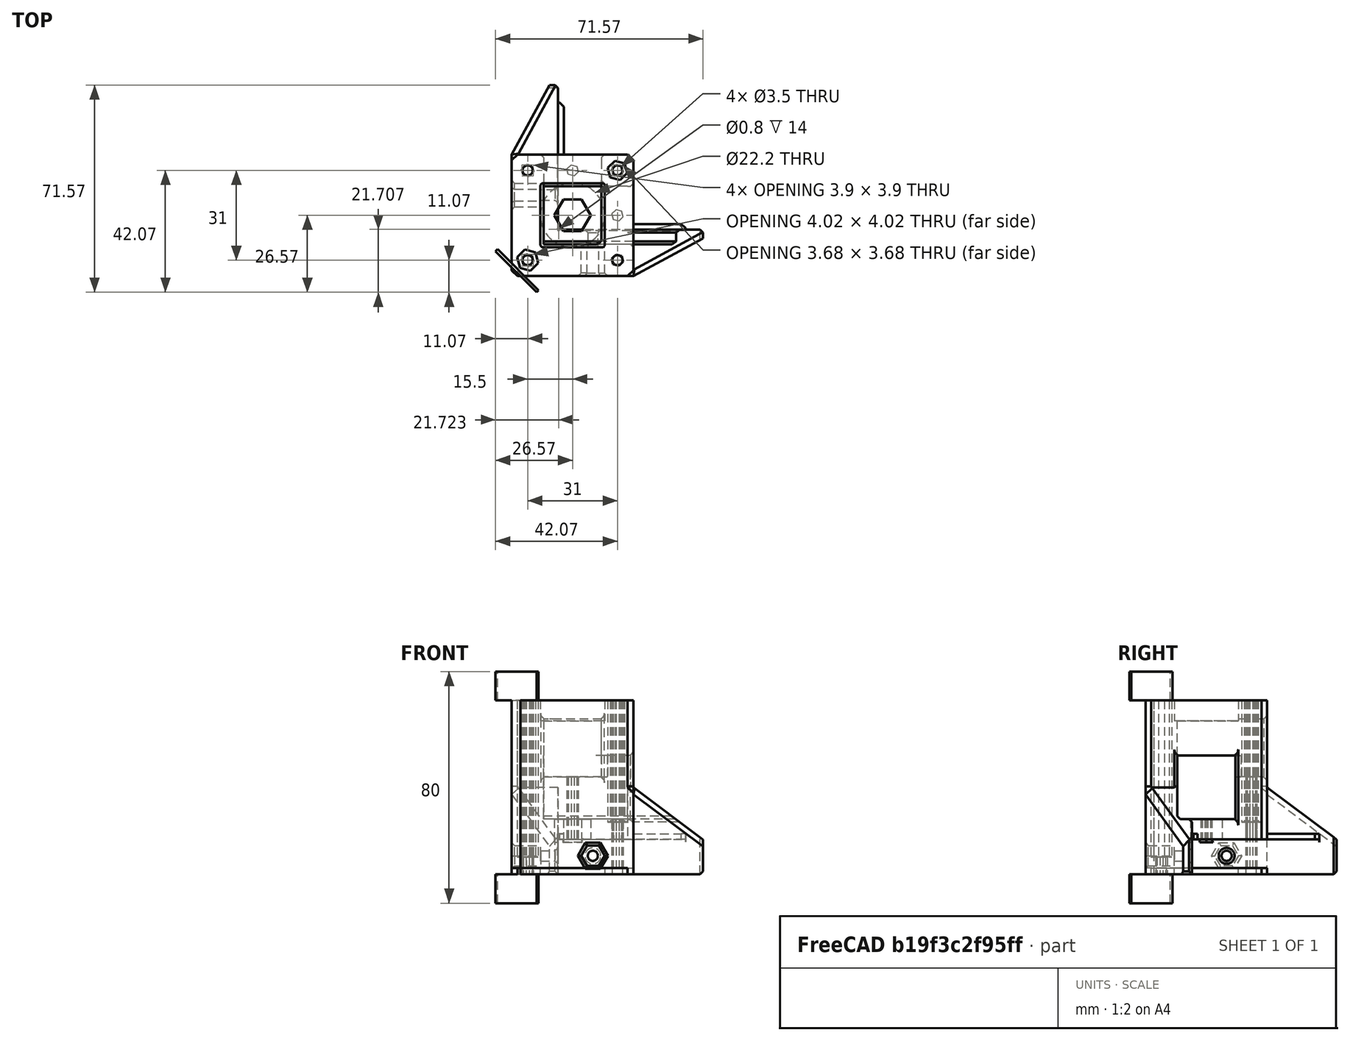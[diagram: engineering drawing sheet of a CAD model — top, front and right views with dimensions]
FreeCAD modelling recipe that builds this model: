
FCSTD DOCUMENT  (FreeCAD 0.19R)
Label: StepperTower_structural
License: All rights reserved
LicenseURL: http://en.wikipedia.org/wiki/All_rights_reserved
objects: Sketcher::SketchObject×27, PartDesign::Pocket×20, PartDesign::Chamfer×18, PartDesign::Fillet×7, PartDesign::Pad×6, PartDesign::Body×2, Mesh::Feature×1
note: 131 computed .brp shape members not serialized (recipe doc carries the construction recipe); baked Part::Feature solids carry a one-line shape summary decoded from their .brp

FEATURE [Sketcher::SketchObject] Sketch  label="wings"
  FullyConstrained = false
  MapMode = 5
  Support = -> [XY_Plane]
  sketch-geometry (21):
    g0: Circle CenterX=5 CenterY=5 CenterZ=0 NormalX=0 NormalY=0 NormalZ=1 AngleXU=0 Radius=2.00199
    g1: LineSegment StartX=-16 StartY=26 StartZ=0 EndX=26 EndY=26 EndZ=0
    g2: LineSegment StartX=26 StartY=26 StartZ=0 EndX=26 EndY=-16 EndZ=0
    g3: LineSegment StartX=26 StartY=-16 StartZ=0 EndX=-16 EndY=-16 EndZ=0
    g4: LineSegment StartX=-16 StartY=-16 StartZ=0 EndX=-16 EndY=26 EndZ=0
    g5: Circle CenterX=20.5 CenterY=20.5 CenterZ=0 NormalX=0 NormalY=0 NormalZ=1 AngleXU=0 Radius=1.5
    g6: Circle CenterX=-10.5 CenterY=20.5 CenterZ=0 NormalX=0 NormalY=0 NormalZ=1 AngleXU=0 Radius=1.5
    g7: Circle CenterX=-10.5 CenterY=-10.5 CenterZ=0 NormalX=0 NormalY=0 NormalZ=1 AngleXU=0 Radius=1.5
    g8: Circle CenterX=20.5 CenterY=-10.5 CenterZ=0 NormalX=0 NormalY=0 NormalZ=1 AngleXU=0 Radius=1.5
    g9: LineSegment StartX=-10.5 StartY=20.5 StartZ=0 EndX=20.5 EndY=20.5 EndZ=0
    g10: LineSegment StartX=20.5 StartY=20.5 StartZ=0 EndX=20.5 EndY=-10.5 EndZ=0
    g11: LineSegment StartX=20.5 StartY=-10.5 StartZ=0 EndX=-10.5 EndY=-10.5 EndZ=0
    g12: LineSegment StartX=-10.5 StartY=-10.5 StartZ=0 EndX=-10.5 EndY=20.5 EndZ=0
    g13: LineSegment StartX=0 StartY=50 StartZ=0 EndX=-3 EndY=50 EndZ=0
    g14: LineSegment StartX=-16 StartY=26 StartZ=0 EndX=-16 EndY=-16 EndZ=0
    g15: LineSegment StartX=-16 StartY=-16 StartZ=0 EndX=26 EndY=-16 EndZ=0
    g16: LineSegment StartX=50 StartY=-3 StartZ=0 EndX=50 EndY=0 EndZ=0
    g17: LineSegment StartX=50 StartY=0 StartZ=0 EndX=0 EndY=0 EndZ=0
    g18: LineSegment StartX=0 StartY=0 StartZ=0 EndX=0 EndY=50 EndZ=0
    g19: LineSegment StartX=-16 StartY=26 StartZ=0 EndX=-3 EndY=50 EndZ=0
    g20: LineSegment StartX=26 StartY=-16 StartZ=0 EndX=50 EndY=-3 EndZ=0
  constraints (55):
    c: DistanceX(g0) = 5
    c: DistanceY(g0) = 5
    c: Coincident(g1,g2)
    c: Coincident(g2,g3)
    c: Coincident(g3,g4)
    c: Coincident(g4,g1)
    c: Horizontal(g1)
    c: Horizontal(g3)
    c: Vertical(g2)
    c: Vertical(g4)
    c: Distance(g1) = 42
    c: Equal(g2,g1)
    c: Symmetric(g1,g3,g0)
    c: Coincident(g9,g6)
    c: Coincident(g9,g5)
    c: Horizontal(g9)
    c: Coincident(g9,g10)
    c: Coincident(g10,g8)
    c: Coincident(g10,g11)
    c: Coincident(g11,g7)
    c: Coincident(g11,g12)
    c: Coincident(g12,g9)
    c: Vertical(g12)
    c: Diameter(g6) = 3
    c: Equal(g6,g5)
    c: Equal(g6,g8)
    c: Equal(g6,g7)
    c: Distance(g11) = 31
    c: Symmetric(g7,g5,g0)
    c: Equal(g11,g12)
    c: Equal(g10,g11)
    c: Equal(g10,g9)
    c: PointOnObject(g13,g-2)
    c: Horizontal(g13)
    c: Vertical(g14)
    c: Coincident(g14,g15)
    c: Horizontal(g15)
    c: Vertical(g16)
    c: Coincident(g16,g17)
    c: Horizontal(g17)
    c: Coincident(g17,g18)
    c: Coincident(g18,g13)
    c: DistanceY(g13) = 50
    c: DistanceX(g16) = 50
    c: DistanceX(g14) = -16
    c: Distance(g13) = 3
    c: Distance(g16) = 3
    c: Coincident(g17,g-1)
    c: DistanceX(g15) = 26
    c: DistanceY(g14) = -16
    c: DistanceY(g14) = 26
    c: Coincident(g19,g14)
    c: Coincident(g19,g13)
    c: Coincident(g20,g15)
    c: Coincident(g20,g16)
FEATURE [Sketcher::SketchObject] Sketch002  label="body"
  FullyConstrained = false
  MapMode = 5
  Placement = pos=(0,0,60) rot=(0,0,1;0rad)
  sketch-geometry (5):
    g0: LineSegment StartX=-16 StartY=26 StartZ=0 EndX=26 EndY=26 EndZ=0
    g1: LineSegment StartX=26 StartY=26 StartZ=0 EndX=26 EndY=-16 EndZ=0
    g2: LineSegment StartX=26 StartY=-16 StartZ=0 EndX=-16 EndY=-16 EndZ=0
    g3: LineSegment StartX=-16 StartY=-16 StartZ=0 EndX=-16 EndY=26 EndZ=0
    g4: Circle CenterX=5 CenterY=5 CenterZ=0 NormalX=0 NormalY=0 NormalZ=1 AngleXU=0 Radius=0.859105
  constraints (13):
    c: Coincident(g0,g1)
    c: Coincident(g1,g2)
    c: Coincident(g2,g3)
    c: Coincident(g3,g0)
    c: Horizontal(g0)
    c: Horizontal(g2)
    c: Vertical(g1)
    c: Vertical(g3)
    c: Distance(g0) = 42
    c: DistanceX(g4) = 5
    c: DistanceY(g4) = 5
    c: Symmetric(g0,g2,g4)
    c: Distance(g1) = 42
FEATURE [Sketcher::SketchObject] Sketch003  label="y-hole"
  FullyConstrained = false
  MapMode = 5
  Placement = pos=(26,0,0) rot=(0.57735,0.57735,0.57735;2.0944rad)
  sketch-geometry (5):
    g0: LineSegment StartX=-5 StartY=41 StartZ=0 EndX=15 EndY=41 EndZ=0
    g1: LineSegment StartX=15 StartY=41 StartZ=0 EndX=15 EndY=19 EndZ=0
    g2: LineSegment StartX=15 StartY=19 StartZ=0 EndX=-5 EndY=19 EndZ=0
    g3: LineSegment StartX=-5 StartY=19 StartZ=0 EndX=-5 EndY=41 EndZ=0
    g4: Circle CenterX=5 CenterY=19 CenterZ=0 NormalX=0 NormalY=0 NormalZ=1 AngleXU=0 Radius=1.08669
  constraints (13):
    c: Coincident(g0,g1)
    c: Coincident(g1,g2)
    c: Coincident(g2,g3)
    c: Coincident(g3,g0)
    c: Horizontal(g0)
    c: Horizontal(g2)
    c: Vertical(g1)
    c: Vertical(g3)
    c: DistanceX(g4) = 5
    c: Symmetric(g1,g2,g4)
    c: DistanceY(g1) = 19
    c: Distance(g1) = 22
    c: Distance(g0) = 20
FEATURE [Sketcher::SketchObject] Sketch004  label="x-hole"
  FullyConstrained = false
  MapMode = 5
  Placement = pos=(0,26,0) rot=(0,0.707107,0.707107;3.14159rad)
  sketch-geometry (5):
    g0: LineSegment StartX=-15 StartY=53.6 StartZ=0 EndX=5 EndY=53.6 EndZ=0
    g1: LineSegment StartX=5 StartY=53.6 StartZ=0 EndX=5 EndY=33.6 EndZ=0
    g2: LineSegment StartX=5 StartY=33.6 StartZ=0 EndX=-15 EndY=33.6 EndZ=0
    g3: LineSegment StartX=-15 StartY=33.6 StartZ=0 EndX=-15 EndY=53.6 EndZ=0
    g4: Circle CenterX=-5 CenterY=33.6 CenterZ=0 NormalX=0 NormalY=0 NormalZ=1 AngleXU=0 Radius=1.47678
  constraints (13):
    c: Coincident(g0,g1)
    c: Coincident(g1,g2)
    c: Coincident(g2,g3)
    c: Coincident(g3,g0)
    c: Horizontal(g0)
    c: Horizontal(g2)
    c: Vertical(g1)
    c: Vertical(g3)
    c: DistanceX(g4) = -5
    c: Symmetric(g1,g2,g4)
    c: Distance(g2) = 20
    c: DistanceY(g1) = 33.6
    c: Distance(g1) = 20
FEATURE [Sketcher::SketchObject] Sketch005  label="RightLholes"
  FullyConstrained = true
  MapMode = 5
  Placement = pos=(0,0,0) rot=(0.57735,0.57735,0.57735;2.0944rad)
  sketch-geometry (2):
    g0: Circle CenterX=12 CenterY=6.35 CenterZ=0 NormalX=0 NormalY=0 NormalZ=1 AngleXU=0 Radius=1.75
    g1: Circle CenterX=37 CenterY=6.35 CenterZ=0 NormalX=0 NormalY=0 NormalZ=1 AngleXU=0 Radius=1.75
  constraints (6):
    c: DistanceY(g0) = 6.35
    c: DistanceX(g0) = 12
    c: Diameter(g0) = 3.5
    c: Distance(g1,g0) = 25
    c: DistanceY(g1) = 6.35
    c: Diameter(g1) = 3.5
FEATURE [Sketcher::SketchObject] Sketch006  label="leftLHoles"
  FullyConstrained = false
  MapMode = 5
  Placement = pos=(0,0,0) rot=(0,0.707107,0.707107;3.14159rad)
  sketch-geometry (6):
    g0: Circle CenterX=-12 CenterY=6.35 CenterZ=0 NormalX=0 NormalY=0 NormalZ=1 AngleXU=0 Radius=1.75
    g1: LineSegment StartX=-7.5 StartY=14.1629 StartZ=0 EndX=-2.5 EndY=14.1629 EndZ=0
    g2: LineSegment StartX=-2.5 StartY=14.1629 StartZ=0 EndX=-2.5 EndY=11.492 EndZ=0
    g3: LineSegment StartX=-2.5 StartY=11.492 StartZ=0 EndX=-7.5 EndY=11.492 EndZ=0
    g4: LineSegment StartX=-7.5 StartY=11.492 StartZ=0 EndX=-7.5 EndY=14.1629 EndZ=0
    g5: Circle CenterX=-37 CenterY=6.35 CenterZ=0 NormalX=0 NormalY=0 NormalZ=1 AngleXU=0 Radius=1.75
  constraints (16):
    c: DistanceX(g0) = -12
    c: DistanceY(g0) = 6.35
    c: Diameter(g0) = 3.5
    c: Coincident(g1,g2)
    c: Coincident(g2,g3)
    c: Coincident(g3,g4)
    c: Coincident(g4,g1)
    c: Horizontal(g1)
    c: Horizontal(g3)
    c: Vertical(g2)
    c: Vertical(g4)
    c: Distance(g3) = 5
    c: DistanceX(g2) = -2.5
    c: Distance(g5,g0) = 25
    c: DistanceY(g5) = 6.35
    c: Diameter(g5) = 3.5
FEATURE [Sketcher::SketchObject] Sketch011  label="bearingHole"
  FullyConstrained = true
  MapMode = 5
  Placement = pos=(0,0,19) rot=(0,0,1;0rad)
  sketch-geometry (7):
    g0: LineSegment StartX=8.14656 StartY=-0.45 StartZ=0 EndX=11.2931 EndY=5 EndZ=0
    g1: LineSegment StartX=11.2931 StartY=5 StartZ=0 EndX=8.14656 EndY=10.45 EndZ=0
    g2: LineSegment StartX=8.14656 StartY=10.45 StartZ=0 EndX=1.85344 EndY=10.45 EndZ=0
    g3: LineSegment StartX=1.85344 StartY=10.45 StartZ=0 EndX=-1.29312 EndY=5 EndZ=0
    g4: LineSegment StartX=-1.29312 StartY=5 StartZ=0 EndX=1.85344 EndY=-0.45 EndZ=0
    g5: LineSegment StartX=1.85344 StartY=-0.45 StartZ=0 EndX=8.14656 EndY=-0.45 EndZ=0
    g6: Circle CenterX=5 CenterY=5 CenterZ=0 NormalX=0 NormalY=0 NormalZ=1 AngleXU=0 Radius=6.29312
  constraints (17):
    c: Coincident(g0,g1)
    c: Coincident(g1,g2)
    c: Coincident(g2,g3)
    c: Coincident(g3,g4)
    c: Coincident(g4,g5)
    c: Coincident(g5,g0)
    c: Equal(g0, g1-g5) x5
    c: PointOnObject(g0,g6)
    c: PointOnObject(g1,g6)
    c: PointOnObject(g2,g6)
    c: PointOnObject(g3,g6)
    c: PointOnObject(g4,g6)
    c: PointOnObject(g5,g6)
    c: Distance(g0,g3) = 10.9
    c: Horizontal(g5)
    c: DistanceX(g6) = 5
    c: DistanceY(g6) = 5
FEATURE [Sketcher::SketchObject] Sketch018  label="FrontStepperBoltClear"
  FullyConstrained = false
  MapMode = 5
  Placement = pos=(0,0,59.7) rot=(0,0,1;0rad)
  sketch-geometry (11):
    g0: Circle CenterX=-10.5 CenterY=20.5 CenterZ=0 NormalX=0 NormalY=0 NormalZ=1 AngleXU=0 Radius=1.4
    g1: Circle CenterX=20.5 CenterY=-10.5 CenterZ=0 NormalX=0 NormalY=0 NormalZ=1 AngleXU=0 Radius=1.4
    g2: Circle CenterX=5 CenterY=5 CenterZ=0 NormalX=0 NormalY=0 NormalZ=1 AngleXU=0 Radius=0.593527
    g3: Circle CenterX=-10.5 CenterY=-10.5 CenterZ=0 NormalX=0 NormalY=0 NormalZ=1 AngleXU=0 Radius=1.75
    g4: LineSegment StartX=20.9931 StartY=18.6597 StartZ=0 EndX=22.3403 EndY=20.0069 EndZ=0
    g5: LineSegment StartX=22.3403 StartY=20.0069 StartZ=0 EndX=21.8472 EndY=21.8472 EndZ=0
    g6: LineSegment StartX=21.8472 StartY=21.8472 StartZ=0 EndX=20.0069 EndY=22.3403 EndZ=0
    g7: LineSegment StartX=20.0069 StartY=22.3403 StartZ=0 EndX=18.6597 EndY=20.9931 EndZ=0
    g8: LineSegment StartX=18.6597 StartY=20.9931 StartZ=0 EndX=19.1528 EndY=19.1528 EndZ=0
    g9: LineSegment StartX=19.1528 StartY=19.1528 StartZ=0 EndX=20.9931 EndY=18.6597 EndZ=0
    g10: Circle CenterX=20.5 CenterY=20.5 CenterZ=0 NormalX=0 NormalY=0 NormalZ=1 AngleXU=0 Radius=1.90526
  constraints (27):
    c: Diameter(g0) = 2.8
    c: Diameter(g1) = 2.8
    c: DistanceX(g2) = 5
    c: DistanceY(g2) = 5
    c: Symmetric(g1,g0,g2)
    c: DistanceY(g0) = 20.5
    c: DistanceX(g0) = -10.5
    c: DistanceX(g3) = -10.5
    c: DistanceY(g3) = -10.5
    c: Diameter(g3) = 3.5
    c: Coincident(g4,g5)
    c: Coincident(g5,g6)
    c: Coincident(g6,g7)
    c: Coincident(g7,g8)
    c: Coincident(g8,g9)
    c: Coincident(g9,g4)
    c: Equal(g4, g5-g9) x5
    c: PointOnObject(g4,g10)
    c: PointOnObject(g5,g10)
    c: PointOnObject(g6,g10)
    c: PointOnObject(g7,g10)
    c: PointOnObject(g8,g10)
    c: PointOnObject(g9,g10)
    c: Distance(g8,g4) = 3.3
    c: Angle(g4) = 0.785398
    c: DistanceX(g10) = 20.5
    c: DistanceY(g10) = 20.5
FEATURE [Sketcher::SketchObject] Sketch019  label="countersink2"
  FullyConstrained = true
  MapMode = 5
  Placement = pos=(0,-16,0) rot=(1,0,0;1.5708rad)
  sketch-geometry (14):
    g0: LineSegment StartX=39.0207 StartY=2.85 StartZ=0 EndX=41.0415 EndY=6.35 EndZ=0
    g1: LineSegment StartX=41.0415 StartY=6.35 StartZ=0 EndX=39.0207 EndY=9.85 EndZ=0
    g2: LineSegment StartX=39.0207 StartY=9.85 StartZ=0 EndX=34.9793 EndY=9.85 EndZ=0
    g3: LineSegment StartX=34.9793 StartY=9.85 StartZ=0 EndX=32.9585 EndY=6.35 EndZ=0
    g4: LineSegment StartX=32.9585 StartY=6.35 StartZ=0 EndX=34.9793 EndY=2.85 EndZ=0
    g5: LineSegment StartX=34.9793 StartY=2.85 StartZ=0 EndX=39.0207 EndY=2.85 EndZ=0
    g6: Circle CenterX=37 CenterY=6.35 CenterZ=0 NormalX=0 NormalY=0 NormalZ=1 AngleXU=0 Radius=4.04145
    g7: LineSegment StartX=14.0207 StartY=2.85 StartZ=0 EndX=16.0415 EndY=6.35 EndZ=0
    g8: LineSegment StartX=16.0415 StartY=6.35 StartZ=0 EndX=14.0207 EndY=9.85 EndZ=0
    g9: LineSegment StartX=14.0207 StartY=9.85 StartZ=0 EndX=9.97927 EndY=9.85 EndZ=0
    g10: LineSegment StartX=9.97927 StartY=9.85 StartZ=0 EndX=7.95855 EndY=6.35 EndZ=0
    g11: LineSegment StartX=7.95855 StartY=6.35 StartZ=0 EndX=9.97927 EndY=2.85 EndZ=0
    g12: LineSegment StartX=9.97927 StartY=2.85 StartZ=0 EndX=14.0207 EndY=2.85 EndZ=0
    g13: Circle CenterX=12 CenterY=6.35 CenterZ=0 NormalX=0 NormalY=0 NormalZ=1 AngleXU=0 Radius=4.04145
  constraints (34):
    c: Coincident(g0,g1)
    c: Coincident(g1,g2)
    c: Coincident(g2,g3)
    c: Coincident(g3,g4)
    c: Coincident(g4,g5)
    c: Coincident(g5,g0)
    c: Equal(g0, g1-g5) x5
    c: PointOnObject(g0,g6)
    c: PointOnObject(g1,g6)
    c: PointOnObject(g2,g6)
    c: PointOnObject(g3,g6)
    c: PointOnObject(g4,g6)
    c: PointOnObject(g5,g6)
    c: Horizontal(g5)
    c: DistanceY(g6) = 6.35
    c: DistanceX(g6) = 37
    c: Distance(g0,g4) = 7
    c: Coincident(g7,g8)
    c: Coincident(g8,g9)
    c: Coincident(g9,g10)
    c: Coincident(g10,g11)
    c: Coincident(g11,g12)
    c: Coincident(g12,g7)
    c: Equal(g7, g8-g12) x5
    c: PointOnObject(g7,g13)
    c: PointOnObject(g8,g13)
    c: PointOnObject(g9,g13)
    c: PointOnObject(g10,g13)
    c: PointOnObject(g11,g13)
    c: PointOnObject(g12,g13)
    c: Horizontal(g12)
    c: Distance(g7,g11) = 7
    c: DistanceX(g13) = 12
    c: DistanceY(g13) = 6.35
FEATURE [Sketcher::SketchObject] Sketch020  label="countersink1"
  FullyConstrained = true
  MapMode = 5
  Placement = pos=(-16,0,0) rot=(0.57735,-0.57735,-0.57735;2.0944rad)
  sketch-geometry (14):
    g0: LineSegment StartX=-34.9793 StartY=2.85 StartZ=0 EndX=-32.9585 EndY=6.35 EndZ=0
    g1: LineSegment StartX=-32.9585 StartY=6.35 StartZ=0 EndX=-34.9793 EndY=9.85 EndZ=0
    g2: LineSegment StartX=-34.9793 StartY=9.85 StartZ=0 EndX=-39.0207 EndY=9.85 EndZ=0
    g3: LineSegment StartX=-39.0207 StartY=9.85 StartZ=0 EndX=-41.0415 EndY=6.35 EndZ=0
    g4: LineSegment StartX=-41.0415 StartY=6.35 StartZ=0 EndX=-39.0207 EndY=2.85 EndZ=0
    g5: LineSegment StartX=-39.0207 StartY=2.85 StartZ=0 EndX=-34.9793 EndY=2.85 EndZ=0
    g6: Circle CenterX=-37 CenterY=6.35 CenterZ=0 NormalX=0 NormalY=0 NormalZ=1 AngleXU=0 Radius=4.04145
    g7: LineSegment StartX=-9.97927 StartY=2.85 StartZ=0 EndX=-7.95855 EndY=6.35 EndZ=0
    g8: LineSegment StartX=-7.95855 StartY=6.35 StartZ=0 EndX=-9.97927 EndY=9.85 EndZ=0
    g9: LineSegment StartX=-9.97927 StartY=9.85 StartZ=0 EndX=-14.0207 EndY=9.85 EndZ=0
    g10: LineSegment StartX=-14.0207 StartY=9.85 StartZ=0 EndX=-16.0415 EndY=6.35 EndZ=0
    g11: LineSegment StartX=-16.0415 StartY=6.35 StartZ=0 EndX=-14.0207 EndY=2.85 EndZ=0
    g12: LineSegment StartX=-14.0207 StartY=2.85 StartZ=0 EndX=-9.97927 EndY=2.85 EndZ=0
    g13: Circle CenterX=-12 CenterY=6.35 CenterZ=0 NormalX=0 NormalY=0 NormalZ=1 AngleXU=0 Radius=4.04145
  constraints (34):
    c: Coincident(g0,g1)
    c: Coincident(g1,g2)
    c: Coincident(g2,g3)
    c: Coincident(g3,g4)
    c: Coincident(g4,g5)
    c: Coincident(g5,g0)
    c: Equal(g0, g1-g5) x5
    c: PointOnObject(g0,g6)
    c: PointOnObject(g1,g6)
    c: PointOnObject(g2,g6)
    c: PointOnObject(g3,g6)
    c: PointOnObject(g4,g6)
    c: PointOnObject(g5,g6)
    c: Horizontal(g5)
    c: Distance(g0,g3) = 7
    c: DistanceX(g6) = -37
    c: DistanceY(g6) = 6.35
    c: Coincident(g7,g8)
    c: Coincident(g8,g9)
    c: Coincident(g9,g10)
    c: Coincident(g10,g11)
    c: Coincident(g11,g12)
    c: Coincident(g12,g7)
    c: Equal(g7, g8-g12) x5
    c: PointOnObject(g7,g13)
    c: PointOnObject(g8,g13)
    c: PointOnObject(g9,g13)
    c: PointOnObject(g10,g13)
    c: PointOnObject(g11,g13)
    c: PointOnObject(g12,g13)
    c: Horizontal(g12)
    c: Distance(g7,g10) = 7
    c: DistanceX(g13) = -12
    c: DistanceY(g13) = 6.35
FEATURE [Sketcher::SketchObject] Sketch024
  FullyConstrained = false
  MapMode = 5
  Support = -> [XY_Plane001]
  sketch-geometry (5):
    g0: LineSegment StartX=-16 StartY=26 StartZ=0 EndX=26 EndY=26 EndZ=0
    g1: LineSegment StartX=26 StartY=26 StartZ=0 EndX=26 EndY=-16 EndZ=0
    g2: LineSegment StartX=26 StartY=-16 StartZ=0 EndX=-16 EndY=-16 EndZ=0
    g3: LineSegment StartX=-16 StartY=-16 StartZ=0 EndX=-16 EndY=26 EndZ=0
    g4: Circle CenterX=5 CenterY=5 CenterZ=0 NormalX=0 NormalY=0 NormalZ=1 AngleXU=0 Radius=1.67343
  constraints (13):
    c: Coincident(g0,g1)
    c: Coincident(g1,g2)
    c: Coincident(g2,g3)
    c: Coincident(g3,g0)
    c: Horizontal(g0)
    c: Horizontal(g2)
    c: Vertical(g1)
    c: Vertical(g3)
    c: Equal(g0,g1)
    c: Distance(g1) = 42
    c: DistanceX(g4) = 5
    c: DistanceY(g4) = 5
    c: Symmetric(g2,g0,g4)
FEATURE [PartDesign::Pad] Pad002
  Direction = (1,1,1)
  Length = 2.2
  Length2 = 100
  Profile = -> Sketch024
  Type = 0
FEATURE [Sketcher::SketchObject] Sketch025
  FullyConstrained = true
  MapMode = 5
  Placement = pos=(0,0,2.2) rot=(0,0,1;0rad)
  Support = -> [Pad002]
  sketch-geometry (1):
    g0: Circle CenterX=5 CenterY=5 CenterZ=0 NormalX=0 NormalY=0 NormalZ=1 AngleXU=0 Radius=11.1
  constraints (3):
    c: DistanceX(g0) = 5
    c: DistanceY(g0) = 5
    c: Diameter(g0) = 22.2
FEATURE [PartDesign::Pocket] Pocket012
  BaseFeature = -> Pad002
  Length = 5
  Length2 = 100
  Profile = -> Sketch025
  Type = 0
FEATURE [PartDesign::Chamfer] Chamfer
  Angle = 45
  Base = -> Pocket012 [Edge2,Edge8,Edge5,Edge1]
  BaseFeature = -> Pocket012
  ChamferType = 0
  FlipDirection = false
  Size = 2
  Size2 = 1
  SupportTransform = false
FEATURE [Sketcher::SketchObject] Sketch026
  FullyConstrained = false
  MapMode = 5
  Placement = pos=(0,0,2.2) rot=(0,0,1;0rad)
  Support = -> [Chamfer]
  sketch-geometry (9):
    g0: Circle CenterX=-10.5 CenterY=20.5 CenterZ=0 NormalX=0 NormalY=0 NormalZ=1 AngleXU=0 Radius=1.75
    g1: Circle CenterX=20.5 CenterY=20.5 CenterZ=0 NormalX=0 NormalY=0 NormalZ=1 AngleXU=0 Radius=1.75
    g2: Circle CenterX=20.5 CenterY=-10.5 CenterZ=0 NormalX=0 NormalY=0 NormalZ=1 AngleXU=0 Radius=1.75
    g3: Circle CenterX=-10.5 CenterY=-10.5 CenterZ=0 NormalX=0 NormalY=0 NormalZ=1 AngleXU=0 Radius=1.75
    g4: LineSegment StartX=-10.5 StartY=20.5 StartZ=0 EndX=20.5 EndY=20.5 EndZ=0
    g5: LineSegment StartX=20.5 StartY=20.5 StartZ=0 EndX=20.5 EndY=-10.5 EndZ=0
    g6: LineSegment StartX=20.5 StartY=-10.5 StartZ=0 EndX=-10.5 EndY=-10.5 EndZ=0
    g7: LineSegment StartX=-10.5 StartY=-10.5 StartZ=0 EndX=-10.5 EndY=20.5 EndZ=0
    g8: Circle CenterX=5 CenterY=5 CenterZ=0 NormalX=0 NormalY=0 NormalZ=1 AngleXU=0 Radius=0.497796
  constraints (21):
    c: Coincident(g4,g0)
    c: Coincident(g4,g1)
    c: Horizontal(g4)
    c: Coincident(g4,g5)
    c: Coincident(g5,g2)
    c: Coincident(g5,g6)
    c: Horizontal(g6)
    c: Coincident(g6,g7)
    c: Coincident(g7,g4)
    c: Vertical(g7)
    c: Coincident(g3,g6)
    c: Equal(g5,g4)
    c: Distance(g4) = 31
    c: DistanceX(g8) = 5
    c: DistanceY(g8) = 5
    c: Symmetric(g3,g1,g8)
    c: Vertical(g5)
    c: Diameter(g1) = 3.5
    c: Equal(g1,g0)
    c: Equal(g1,g3)
    c: Equal(g1,g2)
FEATURE [PartDesign::Pocket] Pocket013
  BaseFeature = -> Chamfer
  Length = 5
  Length2 = 100
  Profile = -> Sketch026
  Type = 0
FEATURE [PartDesign::Body] Body001  label="Washer"
  Group = -> [Sketch024,Pad002,Sketch025,Pocket012,Chamfer,Sketch026,Pocket013]
  Origin = -> Origin001
  Tip = -> Pocket013
FEATURE [PartDesign::Pad] Pad
  Direction = (1,1,1)
  Length = 60
  Length2 = 100
  Profile = -> Sketch
  Type = 0
FEATURE [PartDesign::Pad] Pad003
  BaseFeature = -> Pad
  Direction = (1,1,1)
  Length = 48
  Length2 = 100
  Profile = -> Sketch002
  Reversed = true
  Type = 0
FEATURE [Sketcher::SketchObject] Sketch032  label="wingcut2"
  FullyConstrained = false
  MapMode = 5
  Placement = pos=(0,0,0) rot=(0.57735,0.57735,0.57735;2.0944rad)
  sketch-geometry (4):
    g0: LineSegment StartX=50 StartY=12 StartZ=0 EndX=26 EndY=30 EndZ=0
    g1: LineSegment StartX=26 StartY=30 StartZ=0 EndX=26 EndY=79.987 EndZ=0
    g2: LineSegment StartX=26 StartY=79.987 StartZ=0 EndX=78.9408 EndY=64.2519 EndZ=0
    g3: LineSegment StartX=78.9408 StartY=64.2519 StartZ=0 EndX=50 EndY=12 EndZ=0
  constraints (9):
    c: Coincident(g0,g1)
    c: Vertical(g1)
    c: Coincident(g1,g2)
    c: Coincident(g2,g3)
    c: Coincident(g3,g0)
    c: DistanceX(g0) = 50
    c: DistanceY(g0) = 12
    c: DistanceX(g0) = 26
    c: DistanceY(g0) = 30
FEATURE [Sketcher::SketchObject] Sketch033  label="WingRidge1"
  FullyConstrained = true
  MapMode = 5
  Placement = pos=(0,26,0) rot=(0,0.707107,0.707107;3.14159rad)
  sketch-geometry (4):
    g0: LineSegment StartX=0 StartY=12 StartZ=0 EndX=-2 EndY=12 EndZ=0
    g1: LineSegment StartX=-2 StartY=12 StartZ=0 EndX=-2 EndY=14 EndZ=0
    g2: LineSegment StartX=-2 StartY=14 StartZ=0 EndX=0 EndY=14 EndZ=0
    g3: LineSegment StartX=0 StartY=14 StartZ=0 EndX=0 EndY=12 EndZ=0
  constraints (12):
    c: PointOnObject(g0,g-2)
    c: Coincident(g0,g1)
    c: Coincident(g1,g2)
    c: PointOnObject(g2,g-2)
    c: Coincident(g2,g3)
    c: Coincident(g3,g0)
    c: Horizontal(g0)
    c: Distance(g0) = 2
    c: Distance(g1) = 2
    c: Vertical(g1)
    c: Distance(g3) = 2
    c: DistanceY(g0) = 12
FEATURE [Sketcher::SketchObject] Sketch034  label="wingridge2"
  FullyConstrained = true
  MapMode = 5
  Placement = pos=(26,0,0) rot=(0.57735,0.57735,0.57735;2.0944rad)
  sketch-geometry (4):
    g0: LineSegment StartX=0 StartY=12 StartZ=0 EndX=2 EndY=12 EndZ=0
    g1: LineSegment StartX=2 StartY=12 StartZ=0 EndX=2 EndY=14 EndZ=0
    g2: LineSegment StartX=2 StartY=14 StartZ=0 EndX=0 EndY=14 EndZ=0
    g3: LineSegment StartX=0 StartY=14 StartZ=0 EndX=0 EndY=12 EndZ=0
  constraints (12):
    c: PointOnObject(g0,g-2)
    c: Coincident(g0,g1)
    c: Coincident(g1,g2)
    c: PointOnObject(g2,g-2)
    c: Coincident(g2,g3)
    c: Coincident(g3,g0)
    c: Horizontal(g0)
    c: Distance(g0) = 2
    c: Distance(g1) = 2
    c: Vertical(g1)
    c: Distance(g3) = 2
    c: DistanceY(g0) = 12
FEATURE [PartDesign::Pad] Pad004
  BaseFeature = -> Pad003
  Direction = (1,1,1)
  Length = 18
  Length2 = 100
  Profile = -> Sketch034
  Type = 0
FEATURE [PartDesign::Pad] Pad005
  BaseFeature = -> Pad004
  Direction = (1,1,1)
  Length = 18
  Length2 = 100
  Profile = -> Sketch033
  Type = 0
FEATURE [PartDesign::Pocket] Pocket
  BaseFeature = -> Pad005
  Length = 23
  Length2 = 100
  Profile = -> Sketch032
  Type = 4
FEATURE [Sketcher::SketchObject] Sketch031  label="WingCut1"
  FullyConstrained = false
  MapMode = 5
  Placement = pos=(0,0,0) rot=(0,0.707107,0.707107;3.14159rad)
  Support = -> [Pocket]
  sketch-geometry (4):
    g0: LineSegment StartX=-50 StartY=12 StartZ=0 EndX=-26 EndY=30 EndZ=0
    g1: LineSegment StartX=-26 StartY=30 StartZ=0 EndX=-26 EndY=75.2135 EndZ=0
    g2: LineSegment StartX=-26 StartY=75.2135 StartZ=0 EndX=-50 EndY=66.3047 EndZ=0
    g3: LineSegment StartX=-50 StartY=66.3047 StartZ=0 EndX=-50 EndY=12 EndZ=0
  constraints (10):
    c: Coincident(g0,g1)
    c: Vertical(g1)
    c: Coincident(g1,g2)
    c: Coincident(g2,g3)
    c: Coincident(g3,g0)
    c: Vertical(g3)
    c: DistanceY(g0) = 12
    c: DistanceX(g0) = -50
    c: DistanceX(g0) = -26
    c: DistanceY(g0) = 30
FEATURE [PartDesign::Pocket] Pocket014
  BaseFeature = -> Pocket
  Length = 5
  Length2 = 100
  Profile = -> Sketch031
  Type = 1
FEATURE [PartDesign::Pocket] Pocket015
  BaseFeature = -> Pocket014
  Length = 31
  Length2 = 100
  Profile = -> Sketch003
  Type = 4
FEATURE [PartDesign::Pocket] Pocket016
  BaseFeature = -> Pocket015
  Length = 31
  Length2 = 100
  Profile = -> Sketch004
  Type = 0
FEATURE [PartDesign::Pocket] Pocket017
  BaseFeature = -> Pocket016
  Length = 5
  Length2 = 100
  Profile = -> Sketch005
  Type = 1
FEATURE [PartDesign::Pocket] Pocket018
  BaseFeature = -> Pocket017
  Length = 5
  Length2 = 100
  Profile = -> Sketch006
  Type = 1
FEATURE [PartDesign::Pocket] Pocket019
  BaseFeature = -> Pocket018
  Length = 10
  Length2 = 100
  Profile = -> Sketch020
  Type = 0
FEATURE [PartDesign::Pocket] Pocket020
  BaseFeature = -> Pocket019
  Length = 10
  Length2 = 100
  Profile = -> Sketch019
  Type = 0
FEATURE [PartDesign::Pocket] Pocket021
  BaseFeature = -> Pocket020
  Length = 8
  Length2 = 100
  Profile = -> Sketch011
  Type = 0
FEATURE [Sketcher::SketchObject] Sketch016  label="stepperboss"
  FullyConstrained = false
  MapMode = 5
  Placement = pos=(0,0,60) rot=(0,0,1;0rad)
  Support = -> [Pocket021]
  sketch-geometry (5):
    g0: LineSegment StartX=-6.1 StartY=16.1 StartZ=0 EndX=16.1 EndY=16.1 EndZ=0
    g1: LineSegment StartX=16.1 StartY=16.1 StartZ=0 EndX=16.1 EndY=-6.1 EndZ=0
    g2: LineSegment StartX=16.1 StartY=-6.1 StartZ=0 EndX=-6.1 EndY=-6.1 EndZ=0
    g3: LineSegment StartX=-6.1 StartY=-6.1 StartZ=0 EndX=-6.1 EndY=16.1 EndZ=0
    g4: Circle CenterX=5 CenterY=5 CenterZ=0 NormalX=0 NormalY=0 NormalZ=1 AngleXU=0 Radius=1.21473
  constraints (13):
    c: Coincident(g0,g1)
    c: Coincident(g1,g2)
    c: Coincident(g2,g3)
    c: Coincident(g3,g0)
    c: Horizontal(g0)
    c: Horizontal(g2)
    c: Vertical(g1)
    c: Vertical(g3)
    c: Distance(g3) = 22.2
    c: Equal(g3,g0)
    c: Symmetric(g0,g2,g4)
    c: DistanceY(g4) = 5
    c: DistanceX(g4) = 5
FEATURE [PartDesign::Pocket] Pocket022
  BaseFeature = -> Pocket021
  Length = 7
  Length2 = 100
  Profile = -> Sketch016
  Type = 0
FEATURE [Sketcher::SketchObject] Sketch035  label="stepperClearanceHoles"
  FullyConstrained = true
  MapMode = 5
  Placement = pos=(0,0,60) rot=(0,0,1;0rad)
  Support = -> [Pocket022]
  sketch-geometry (21):
    g0: LineSegment StartX=-8.54813 StartY=19.977 StartZ=0 EndX=-9.07113 EndY=21.9289 EndZ=0
    g1: LineSegment StartX=-9.07113 StartY=21.9289 StartZ=0 EndX=-11.023 EndY=22.4519 EndZ=0
    g2: LineSegment StartX=-11.023 StartY=22.4519 StartZ=0 EndX=-12.4519 EndY=21.023 EndZ=0
    g3: LineSegment StartX=-12.4519 StartY=21.023 StartZ=0 EndX=-11.9289 EndY=19.0711 EndZ=0
    g4: LineSegment StartX=-11.9289 StartY=19.0711 StartZ=0 EndX=-9.977 EndY=18.5481 EndZ=0
    g5: LineSegment StartX=-9.977 StartY=18.5481 StartZ=0 EndX=-8.54813 EndY=19.977 EndZ=0
    g6: Circle CenterX=-10.5 CenterY=20.5 CenterZ=0 NormalX=0 NormalY=0 NormalZ=1 AngleXU=0 Radius=2.02073
    g7: LineSegment StartX=21.023 StartY=-12.4519 StartZ=0 EndX=22.4519 EndY=-11.023 EndZ=0
    g8: LineSegment StartX=22.4519 StartY=-11.023 StartZ=0 EndX=21.9289 EndY=-9.07113 EndZ=0
    g9: LineSegment StartX=21.9289 StartY=-9.07113 StartZ=0 EndX=19.977 EndY=-8.54813 EndZ=0
    g10: LineSegment StartX=19.977 StartY=-8.54813 StartZ=0 EndX=18.5481 EndY=-9.977 EndZ=0
    g11: LineSegment StartX=18.5481 StartY=-9.977 StartZ=0 EndX=19.0711 EndY=-11.9289 EndZ=0
    g12: LineSegment StartX=19.0711 StartY=-11.9289 StartZ=0 EndX=21.023 EndY=-12.4519 EndZ=0
    g13: Circle CenterX=20.5 CenterY=-10.5 CenterZ=0 NormalX=0 NormalY=0 NormalZ=1 AngleXU=0 Radius=2.02073
    g14: LineSegment StartX=-8.49236 StartY=-11.0379 StartZ=0 EndX=-9.03031 EndY=-9.03031 EndZ=0
    g15: LineSegment StartX=-9.03031 StartY=-9.03031 StartZ=0 EndX=-11.0379 EndY=-8.49236 EndZ=0
    g16: LineSegment StartX=-11.0379 StartY=-8.49236 StartZ=0 EndX=-12.5076 EndY=-9.96205 EndZ=0
    g17: LineSegment StartX=-12.5076 StartY=-9.96205 StartZ=0 EndX=-11.9697 EndY=-11.9697 EndZ=0
    g18: LineSegment StartX=-11.9697 StartY=-11.9697 StartZ=0 EndX=-9.96205 EndY=-12.5076 EndZ=0
    g19: LineSegment StartX=-9.96205 StartY=-12.5076 StartZ=0 EndX=-8.49236 EndY=-11.0379 EndZ=0
    g20: Circle CenterX=-10.5 CenterY=-10.5 CenterZ=0 NormalX=0 NormalY=0 NormalZ=1 AngleXU=0 Radius=2.07846
  constraints (51):
    c: Coincident(g0,g1)
    c: Coincident(g1,g2)
    c: Coincident(g2,g3)
    c: Coincident(g3,g4)
    c: Coincident(g4,g5)
    c: Coincident(g5,g0)
    c: Equal(g0, g1-g5) x5
    c: PointOnObject(g0,g6)
    c: PointOnObject(g1,g6)
    c: PointOnObject(g2,g6)
    c: PointOnObject(g3,g6)
    c: PointOnObject(g4,g6)
    c: PointOnObject(g5,g6)
    c: Coincident(g7,g8)
    c: Coincident(g8,g9)
    c: Coincident(g9,g10)
    c: Coincident(g10,g11)
    c: Coincident(g11,g12)
    c: Coincident(g12,g7)
    c: Equal(g7, g8-g12) x5
    c: PointOnObject(g7,g13)
    c: PointOnObject(g8,g13)
    c: PointOnObject(g9,g13)
    c: PointOnObject(g10,g13)
    c: PointOnObject(g11,g13)
    c: PointOnObject(g12,g13)
    c: Coincident(g14,g15)
    c: Coincident(g15,g16)
    c: Coincident(g16,g17)
    c: Coincident(g17,g18)
    c: Coincident(g18,g19)
    c: Coincident(g19,g14)
    c: Equal(g14, g15-g19) x5
    c: PointOnObject(g14,g20)
    c: PointOnObject(g15,g20)
    c: PointOnObject(g16,g20)
    c: PointOnObject(g17,g20)
    c: PointOnObject(g18,g20)
    c: PointOnObject(g19,g20)
    c: Distance(g0,g3) = 3.5
    c: Distance(g7,g10) = 3.5
    c: Distance(g18,g16) = 3.6
    c: Angle(g19) = 0.785398
    c: Angle(g7) = 0.785398
    c: Angle(g5) = 0.785398
    c: DistanceY(g6) = 20.5
    c: DistanceX(g6) = -10.5
    c: DistanceX(g20) = -10.5
    c: DistanceY(g20) = -10.5
    c: DistanceY(g13) = -10.5
    c: DistanceX(g13) = 20.5
FEATURE [PartDesign::Pocket] Pocket023
  BaseFeature = -> Pocket022
  Length = 5
  Length2 = 100
  Profile = -> Sketch035
  Type = 1
FEATURE [Sketcher::SketchObject] Sketch036  label="cornerStepperBolthead"
  FullyConstrained = true
  MapMode = 5
  Placement = pos=(0,0,60) rot=(0,0,1;0rad)
  Support = -> [Pocket023]
  sketch-geometry (7):
    g0: LineSegment StartX=-6.8751 StartY=-11.4713 StartZ=0 EndX=-7.84639 EndY=-7.84639 EndZ=0
    g1: LineSegment StartX=-7.84639 StartY=-7.84639 StartZ=0 EndX=-11.4713 EndY=-6.8751 EndZ=0
    g2: LineSegment StartX=-11.4713 StartY=-6.8751 StartZ=0 EndX=-14.1249 EndY=-9.52871 EndZ=0
    g3: LineSegment StartX=-14.1249 StartY=-9.52871 StartZ=0 EndX=-13.1536 EndY=-13.1536 EndZ=0
    g4: LineSegment StartX=-13.1536 StartY=-13.1536 StartZ=0 EndX=-9.52871 EndY=-14.1249 EndZ=0
    g5: LineSegment StartX=-9.52871 StartY=-14.1249 StartZ=0 EndX=-6.8751 EndY=-11.4713 EndZ=0
    g6: Circle CenterX=-10.5 CenterY=-10.5 CenterZ=0 NormalX=0 NormalY=0 NormalZ=1 AngleXU=0 Radius=3.75278
  constraints (17):
    c: Coincident(g0,g1)
    c: Coincident(g1,g2)
    c: Coincident(g2,g3)
    c: Coincident(g3,g4)
    c: Coincident(g4,g5)
    c: Coincident(g5,g0)
    c: Equal(g0, g1-g5) x5
    c: PointOnObject(g0,g6)
    c: PointOnObject(g1,g6)
    c: PointOnObject(g2,g6)
    c: PointOnObject(g3,g6)
    c: PointOnObject(g4,g6)
    c: PointOnObject(g5,g6)
    c: Distance(g0,g3) = 6.5
    c: Angle(g5) = 0.785398
    c: DistanceX(g6) = -10.5
    c: DistanceY(g6) = -10.5
FEATURE [PartDesign::Pocket] Pocket024
  BaseFeature = -> Pocket023
  Length = 54
  Length2 = 100
  Profile = -> Sketch036
  Type = 0
FEATURE [Sketcher::SketchObject] Sketch037  label="MountBoltsNew"
  FullyConstrained = true
  MapMode = 5
  Placement = pos=(0,7.5e-15,33.6) rot=(0,0,1;0rad)
  Support = -> [Pocket024]
  sketch-geometry (14):
    g0: LineSegment StartX=5.523 StartY=18.5481 StartZ=0 EndX=6.95187 EndY=19.977 EndZ=0
    g1: LineSegment StartX=6.95187 StartY=19.977 StartZ=0 EndX=6.42887 EndY=21.9289 EndZ=0
    g2: LineSegment StartX=6.42887 StartY=21.9289 StartZ=0 EndX=4.477 EndY=22.4519 EndZ=0
    g3: LineSegment StartX=4.477 StartY=22.4519 StartZ=0 EndX=3.04813 EndY=21.023 EndZ=0
    g4: LineSegment StartX=3.04813 StartY=21.023 StartZ=0 EndX=3.57113 EndY=19.0711 EndZ=0
    g5: LineSegment StartX=3.57113 StartY=19.0711 StartZ=0 EndX=5.523 EndY=18.5481 EndZ=0
    g6: Circle CenterX=5 CenterY=20.5 CenterZ=0 NormalX=0 NormalY=0 NormalZ=1 AngleXU=0 Radius=2.02073
    g7: LineSegment StartX=21.023 StartY=3.04813 StartZ=0 EndX=22.4519 EndY=4.477 EndZ=0
    g8: LineSegment StartX=22.4519 StartY=4.477 StartZ=0 EndX=21.9289 EndY=6.42887 EndZ=0
    g9: LineSegment StartX=21.9289 StartY=6.42887 StartZ=0 EndX=19.977 EndY=6.95187 EndZ=0
    g10: LineSegment StartX=19.977 StartY=6.95187 StartZ=0 EndX=18.5481 EndY=5.523 EndZ=0
    g11: LineSegment StartX=18.5481 StartY=5.523 StartZ=0 EndX=19.0711 EndY=3.57113 EndZ=0
    g12: LineSegment StartX=19.0711 StartY=3.57113 StartZ=0 EndX=21.023 EndY=3.04813 EndZ=0
    g13: Circle CenterX=20.5 CenterY=5 CenterZ=0 NormalX=0 NormalY=0 NormalZ=1 AngleXU=0 Radius=2.02073
  constraints (34):
    c: Coincident(g0,g1)
    c: Coincident(g1,g2)
    c: Coincident(g2,g3)
    c: Coincident(g3,g4)
    c: Coincident(g4,g5)
    c: Coincident(g5,g0)
    c: Equal(g0, g1-g5) x5
    c: PointOnObject(g0,g6)
    c: PointOnObject(g1,g6)
    c: PointOnObject(g2,g6)
    c: PointOnObject(g3,g6)
    c: PointOnObject(g4,g6)
    c: PointOnObject(g5,g6)
    c: Coincident(g7,g8)
    c: Coincident(g8,g9)
    c: Coincident(g9,g10)
    c: Coincident(g10,g11)
    c: Coincident(g11,g12)
    c: Coincident(g12,g7)
    c: Equal(g7, g8-g12) x5
    c: PointOnObject(g7,g13)
    c: PointOnObject(g8,g13)
    c: PointOnObject(g9,g13)
    c: PointOnObject(g10,g13)
    c: PointOnObject(g11,g13)
    c: PointOnObject(g12,g13)
    c: DistanceY(g13) = 5
    c: DistanceX(g6) = 5
    c: Angle(g7) = 0.785398
    c: Angle(g0) = 0.785398
    c: Distance(g0,g4) = 3.5
    c: Distance(g7,g11) = 3.5
    c: DistanceX(g13) = 20.5
    c: DistanceY(g6) = 20.5
FEATURE [PartDesign::Pocket] Pocket025
  BaseFeature = -> Pocket024
  Length = 5
  Length2 = 100
  Profile = -> Sketch037
  Type = 1
FEATURE [Sketcher::SketchObject] Sketch021  label="FrontstepperboltHead"
  FullyConstrained = true
  MapMode = 5
  Placement = pos=(0,0,60) rot=(0,0,1;0rad)
  Support = -> [Pocket025]
  sketch-geometry (8):
    g0: Circle CenterX=-10.5 CenterY=-10.5 CenterZ=0 NormalX=0 NormalY=0 NormalZ=1 AngleXU=0 Radius=3.5
    g1: LineSegment StartX=21.3966 StartY=17.1539 StartZ=0 EndX=23.8461 EndY=19.6034 EndZ=0
    g2: LineSegment StartX=23.8461 StartY=19.6034 StartZ=0 EndX=22.9495 EndY=22.9495 EndZ=0
    g3: LineSegment StartX=22.9495 StartY=22.9495 StartZ=0 EndX=19.6034 EndY=23.8461 EndZ=0
    g4: LineSegment StartX=19.6034 StartY=23.8461 StartZ=0 EndX=17.1539 EndY=21.3966 EndZ=0
    g5: LineSegment StartX=17.1539 StartY=21.3966 StartZ=0 EndX=18.0505 EndY=18.0505 EndZ=0
    g6: LineSegment StartX=18.0505 StartY=18.0505 StartZ=0 EndX=21.3966 EndY=17.1539 EndZ=0
    g7: Circle CenterX=20.5 CenterY=20.5 CenterZ=0 NormalX=0 NormalY=0 NormalZ=1 AngleXU=0 Radius=3.4641
  constraints (20):
    c: DistanceX(g0) = -10.5
    c: DistanceY(g0) = -10.5
    c: Diameter(g0) = 7
    c: Coincident(g1,g2)
    c: Coincident(g2,g3)
    c: Coincident(g3,g4)
    c: Coincident(g4,g5)
    c: Coincident(g5,g6)
    c: Coincident(g6,g1)
    c: Equal(g1, g2-g6) x5
    c: PointOnObject(g1,g7)
    c: PointOnObject(g2,g7)
    c: PointOnObject(g3,g7)
    c: PointOnObject(g4,g7)
    c: PointOnObject(g5,g7)
    c: PointOnObject(g6,g7)
    c: DistanceY(g7) = 20.5
    c: DistanceX(g7) = 20.5
    c: Distance(g5,g1) = 6
    c: Angle(g1) = 0.785398
FEATURE [PartDesign::Pocket] Pocket026
  BaseFeature = -> Pocket025
  Length = 42
  Length2 = 100
  Profile = -> Sketch021
  Type = 0
FEATURE [PartDesign::Pocket] Pocket027
  BaseFeature = -> Pocket026
  Length = 5
  Length2 = 100
  Profile = -> Sketch018
  Type = 1
FEATURE [PartDesign::Chamfer] Chamfer001
  Angle = 45
  Base = -> Pocket027 [Edge329]
  BaseFeature = -> Pocket027
  ChamferType = 0
  FlipDirection = false
  Size = 2
  Size2 = 1
  SupportTransform = false
FEATURE [PartDesign::Chamfer] Chamfer002
  Angle = 45
  Base = -> Chamfer001 [Edge28]
  BaseFeature = -> Chamfer001
  ChamferType = 0
  FlipDirection = false
  Size = 2
  Size2 = 1
  SupportTransform = false
FEATURE [PartDesign::Chamfer] Chamfer003
  Angle = 45
  Base = -> Chamfer002 [Edge113]
  BaseFeature = -> Chamfer002
  ChamferType = 0
  FlipDirection = false
  Size = 3
  Size2 = 1
  SupportTransform = false
FEATURE [PartDesign::Chamfer] Chamfer004
  Angle = 45
  Base = -> Chamfer003 [Edge119,Edge33]
  BaseFeature = -> Chamfer003
  ChamferType = 0
  FlipDirection = false
  Size = 2
  Size2 = 1
  SupportTransform = false
FEATURE [PartDesign::Chamfer] Chamfer005
  Angle = 45
  Base = -> Chamfer004 [Edge164,Edge49]
  BaseFeature = -> Chamfer004
  ChamferType = 0
  FlipDirection = false
  Size = 2
  Size2 = 1
  SupportTransform = false
FEATURE [Sketcher::SketchObject] Sketch038
  FullyConstrained = true
  MapMode = 5
  Placement = pos=(-14.5,-14.5,0) rot=(0.862856,-0.357407,-0.357407;1.71777rad)
  Support = -> [Chamfer005]
  sketch-geometry (8):
    g0: LineSegment StartX=-10 StartY=70 StartZ=0 EndX=10 EndY=70 EndZ=0
    g1: LineSegment StartX=10 StartY=70 StartZ=0 EndX=10 EndY=60 EndZ=0
    g2: LineSegment StartX=10 StartY=60 StartZ=0 EndX=-10 EndY=60 EndZ=0
    g3: LineSegment StartX=-10 StartY=60 StartZ=0 EndX=-10 EndY=70 EndZ=0
    g4: LineSegment StartX=-10 StartY=0 StartZ=0 EndX=10 EndY=0 EndZ=0
    g5: LineSegment StartX=10 StartY=0 StartZ=0 EndX=10 EndY=-10 EndZ=0
    g6: LineSegment StartX=10 StartY=-10 StartZ=0 EndX=-10 EndY=-10 EndZ=0
    g7: LineSegment StartX=-10 StartY=-10 StartZ=0 EndX=-10 EndY=0 EndZ=0
  constraints (22):
    c: Coincident(g0,g1)
    c: Coincident(g1,g2)
    c: Coincident(g2,g3)
    c: Coincident(g3,g0)
    c: Horizontal(g0)
    c: Vertical(g1)
    c: Vertical(g3)
    c: Coincident(g4,g5)
    c: Coincident(g5,g6)
    c: Coincident(g6,g7)
    c: Coincident(g7,g4)
    c: Horizontal(g4)
    c: Vertical(g5)
    c: Vertical(g7)
    c: Distance(g1) = 10
    c: Distance(g5) = 10
    c: Distance(g4) = 20
    c: Distance(g0) = 20
    c: Symmetric(g1,g2,g-2)
    c: Symmetric(g5,g6,g-2)
    c: DistanceY(g1) = 60
    c: DistanceY(g4) = 0
FEATURE [PartDesign::Pad] Pad006
  BaseFeature = -> Chamfer005
  Direction = (1,1,1)
  Length = 1
  Length2 = 100
  Profile = -> Sketch038
  Reversed = true
  Type = 0
FEATURE [Sketcher::SketchObject] Sketch039
  FullyConstrained = false
  MapMode = 5
  Placement = pos=(0,44,0) rot=(0,0.707107,0.707107;3.14159rad)
  Support = -> [Pad006]
  sketch-geometry (1):
    g0: Circle CenterX=-0.151459 CenterY=11.836 CenterZ=0 NormalX=0 NormalY=0 NormalZ=1 AngleXU=0 Radius=0.375
  constraints (1):
    c: Diameter(g0) = 0.75
FEATURE [PartDesign::Pocket] Pocket028
  BaseFeature = -> Pad006
  Length = 38
  Length2 = 100
  Profile = -> Sketch039
  Type = 0
FEATURE [Sketcher::SketchObject] Sketch040
  FullyConstrained = false
  MapMode = 5
  Placement = pos=(44,0,0) rot=(0.57735,0.57735,0.57735;2.0944rad)
  Support = -> [Pocket028]
  sketch-geometry (1):
    g0: Circle CenterX=0.149498 CenterY=11.8569 CenterZ=0 NormalX=0 NormalY=0 NormalZ=1 AngleXU=0 Radius=0.375
  constraints (1):
    c: Diameter(g0) = 0.75
FEATURE [PartDesign::Pocket] Pocket029
  BaseFeature = -> Pocket028
  Length = 39
  Length2 = 100
  Profile = -> Sketch040
  Type = 0
FEATURE [Sketcher::SketchObject] Sketch041
  FullyConstrained = false
  MapMode = 5
  Placement = pos=(0,0,0) rot=(1,0,0;3.14159rad)
  Support = -> [Pocket029]
  sketch-geometry (1):
    g0: Circle CenterX=0.153431 CenterY=-0.13663 CenterZ=0 NormalX=0 NormalY=0 NormalZ=1 AngleXU=0 Radius=0.4
  constraints (1):
    c: Diameter(g0) = 0.8
FEATURE [PartDesign::Pocket] Pocket030
  BaseFeature = -> Pocket029
  Length = 14
  Length2 = 100
  Profile = -> Sketch041
  Type = 0
FEATURE [Sketcher::SketchObject] Sketch042
  FullyConstrained = false
  MapMode = 5
  Placement = pos=(0,0,12) rot=(1,0,0;3.14159rad)
  Support = -> [Pocket030]
  sketch-geometry (1):
    g0: Circle CenterX=1.47746 CenterY=-1.26246 CenterZ=0 NormalX=0 NormalY=0 NormalZ=1 AngleXU=0 Radius=2.19764
FEATURE [PartDesign::Fillet] Fillet
  Base = -> Pocket030 [Edge345,Edge340,Edge280,Edge275]
  BaseFeature = -> Pocket030
  Radius = 1
  SupportTransform = false
FEATURE [PartDesign::Fillet] Fillet001
  Base = -> Fillet [Edge309,Edge306]
  BaseFeature = -> Fillet
  Radius = 1
  SupportTransform = false
FEATURE [PartDesign::Fillet] Fillet002
  Base = -> Fillet001 [Edge101,Edge65]
  BaseFeature = -> Fillet001
  Radius = 2
  SupportTransform = false
FEATURE [PartDesign::Chamfer] Chamfer006
  Angle = 45
  Base = -> Fillet002 [Edge387,Edge132]
  BaseFeature = -> Fillet002
  ChamferType = 0
  FlipDirection = false
  Size = 1.5
  Size2 = 1
  SupportTransform = false
FEATURE [PartDesign::Chamfer] Chamfer007
  Angle = 45
  Base = -> Chamfer006 [Edge135,Edge132]
  BaseFeature = -> Chamfer006
  ChamferType = 0
  FlipDirection = false
  Size = 1
  Size2 = 1
  SupportTransform = false
FEATURE [PartDesign::Chamfer] Chamfer008
  Angle = 45
  Base = -> Chamfer007 [Edge63]
  BaseFeature = -> Chamfer007
  ChamferType = 0
  FlipDirection = false
  Size = 1
  Size2 = 1
  SupportTransform = false
FEATURE [PartDesign::Chamfer] Chamfer009
  Angle = 45
  Base = -> Chamfer008 [Edge27]
  BaseFeature = -> Chamfer008
  ChamferType = 0
  FlipDirection = false
  Size = 1
  Size2 = 1
  SupportTransform = false
FEATURE [PartDesign::Chamfer] Chamfer010
  Angle = 45
  Base = -> Chamfer009 [Edge267,Edge50]
  BaseFeature = -> Chamfer009
  ChamferType = 0
  FlipDirection = false
  Size = 1
  Size2 = 1
  SupportTransform = false
FEATURE [PartDesign::Chamfer] Chamfer011
  Angle = 45
  Base = -> Chamfer010 [Edge186,Edge185,Edge184,Edge183,Edge182,Edge187]
  BaseFeature = -> Chamfer010
  ChamferType = 0
  FlipDirection = false
  Size = 1
  Size2 = 1
  SupportTransform = false
FEATURE [PartDesign::Chamfer] Chamfer012
  Angle = 45
  Base = -> Chamfer011 [Edge133,Edge138,Edge137,Edge136,Edge135,Edge134]
  BaseFeature = -> Chamfer011
  ChamferType = 0
  FlipDirection = false
  Size = 1
  Size2 = 1
  SupportTransform = false
FEATURE [PartDesign::Chamfer] Chamfer013
  Angle = 45
  Base = -> Chamfer012 [Edge92,Edge133]
  BaseFeature = -> Chamfer012
  ChamferType = 0
  FlipDirection = false
  Size = 1
  Size2 = 1
  SupportTransform = false
FEATURE [PartDesign::Fillet] Fillet003
  Base = -> Chamfer013 [Edge111,Edge113]
  BaseFeature = -> Chamfer013
  Radius = 2
  SupportTransform = false
FEATURE [PartDesign::Fillet] Fillet004
  Base = -> Fillet003 [Edge110]
  BaseFeature = -> Fillet003
  Radius = 1
  SupportTransform = false
FEATURE [PartDesign::Fillet] Fillet005
  Base = -> Fillet004 [Edge100]
  BaseFeature = -> Fillet004
  Radius = 2
  SupportTransform = false
FEATURE [PartDesign::Fillet] Fillet006
  Base = -> Fillet005 [Edge47,Edge45,Edge27]
  BaseFeature = -> Fillet005
  Radius = 1
  SupportTransform = false
FEATURE [PartDesign::Chamfer] Chamfer014
  Angle = 45
  Base = -> Fillet006 [Edge53]
  BaseFeature = -> Fillet006
  ChamferType = 0
  FlipDirection = false
  Size = 1
  Size2 = 1
  SupportTransform = false
FEATURE [PartDesign::Chamfer] Chamfer015
  Angle = 45
  Base = -> Chamfer014 [Edge75]
  BaseFeature = -> Chamfer014
  ChamferType = 0
  FlipDirection = false
  Size = 1
  Size2 = 1
  SupportTransform = false
FEATURE [PartDesign::Chamfer] Chamfer016
  Angle = 45
  Base = -> Chamfer015 [Edge82]
  BaseFeature = -> Chamfer015
  ChamferType = 0
  FlipDirection = false
  Size = 1
  Size2 = 1
  SupportTransform = false
FEATURE [PartDesign::Chamfer] Chamfer017
  Angle = 45
  Base = -> Chamfer016 [Edge143]
  BaseFeature = -> Chamfer016
  ChamferType = 0
  FlipDirection = false
  Size = 1
  Size2 = 1
  SupportTransform = false
FEATURE [PartDesign::Body] Body
  Group = -> [Sketch,Sketch002,Sketch003,Sketch004,Sketch005,Sketch006,Sketch011,Sketch016,Sketch018,Sketch019,Sketch020,Sketch021,Pad,Pad003,Sketch031,Sketch032,Sketch033,Sketch034,Pad004,Pad005,Pocket,Sketch035,Sketch036,Sketch037,Pocket014,Pocket015,Pocket016,Pocket017,Pocket018,Pocket019,Pocket020,Pocket021,Pocket022,Pocket023,Pocket024,Pocket025,Pocket026,Pocket027,Chamfer001,Chamfer002,Chamfer003,+30 more]
  Origin = -> Origin
  Tip = -> Chamfer017
FEATURE [Mesh::Feature] Mesh  label="Chamfer017 (Meshed)"
